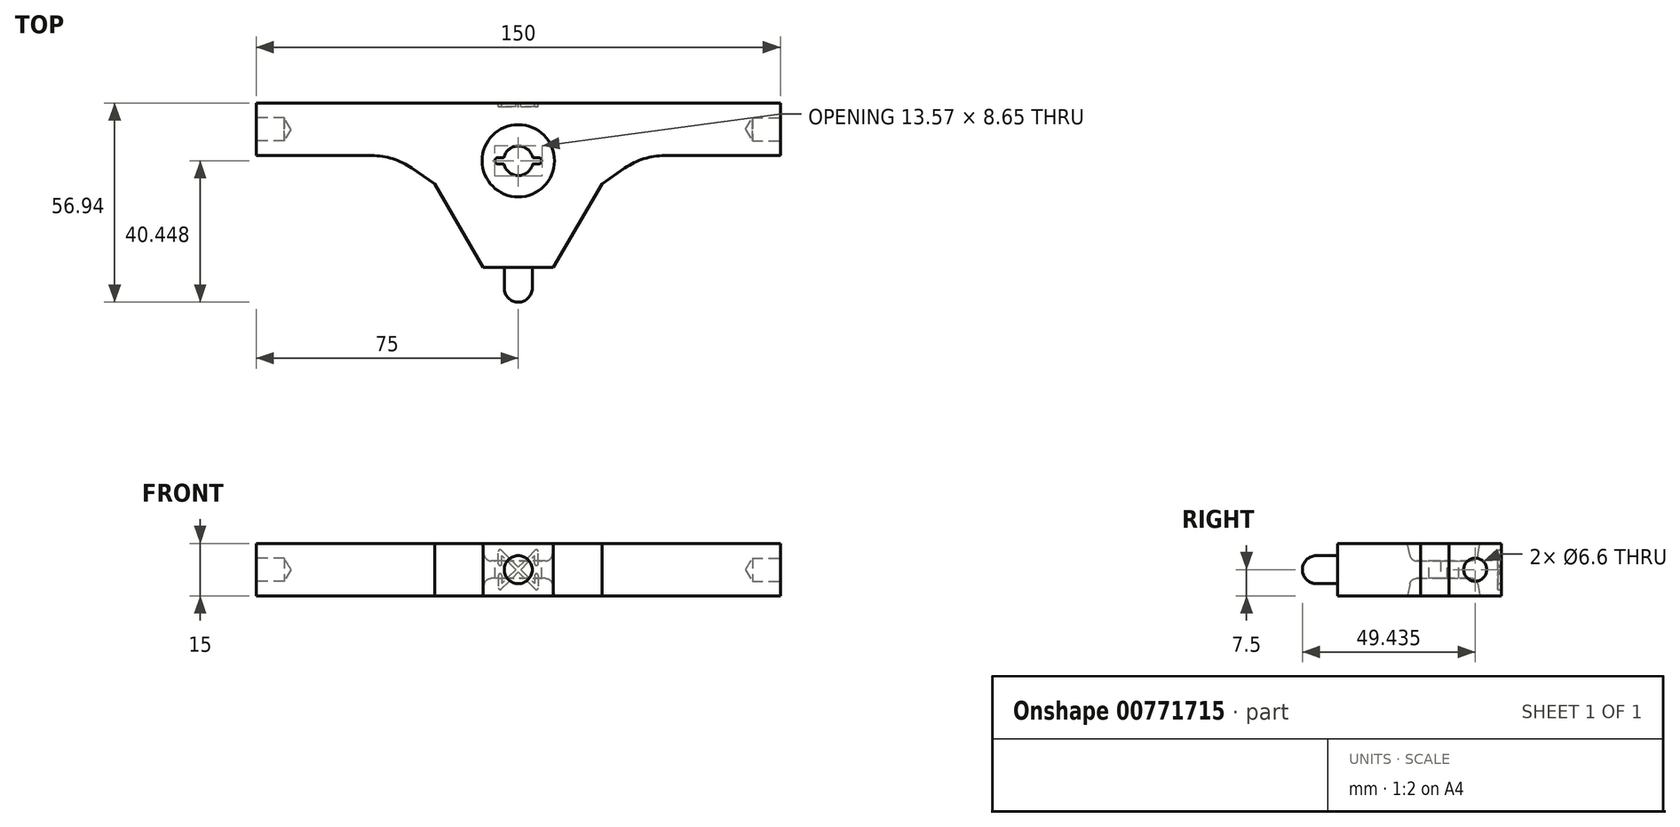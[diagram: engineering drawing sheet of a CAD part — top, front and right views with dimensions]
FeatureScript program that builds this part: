
annotation { "Feature Type Name" : "Feature", "Feature Type Description" : "" }
export const myFeature = defineFeature(function(context is Context, id is Id, definition is map)
    precondition{}
    {
        {
            var Q0;
            Q0=qCreatedBy(makeId("Top.planeOp"),FACE);
            var sketch = newSketch(context, id + "F0", { "sketchPlane" : qUnion([Q0])});
            skLineSegment(sketch, "E0", {"start": v(0, -21.97) * mm, "end": v(0, 24.97) * mm});
            skLineSegment(sketch, "E1", {"start": v(0, 24.97) * mm, "end": v(-75, 24.97) * mm});
            skLineSegment(sketch, "E2", {"start": v(-75, 24.97) * mm, "end": v(-75, 9.97) * mm});
            skLineSegment(sketch, "E3", {"start": v(-75, 9.97) * mm, "end": v(-41.9, 9.97) * mm});
            skLineSegment(sketch, "E4", {"start": v(-30.5, 6.4) * mm, "end": v(-23.93, 1.83) * mm});
            skLineSegment(sketch, "E5", {"start": v(-23.93, 1.83) * mm, "end": v(-10, -21.97) * mm});
            skLineSegment(sketch, "E6", {"start": v(-10, -21.97) * mm, "end": v(0, -21.97) * mm});
            skPoint(sketch, "E7.visualSharp", {"position": v(-35.65, 9.97) * mm});
            skArc(sketch, "E7.filletArc", {"start": v(-30.5, 6.4) * mm, "mid": v(-35.94, 9.05) * mm, "end": v(-41.9, 9.97) * mm});
            skSolve(sketch);
        }
        {
            var Q0;
            Q0=makeQuery(id+"F0.imprint","IMPRINT",FACE,{"disambiguationData":[TD([[makeQuery(id+"F0.imprint","IMPRINT",EDGE,{"derivedFrom":sQuery(id+"F0.wireOp",EDGE,"E0")}),1.0]])]});
            extrude(context, id + "F1", {"entities" : qUnion([Q0]), "depth" : 7.5 * mm, "offsetDistance" : 25 * mm});
        }
        {
            var Q0;
            {var subQ0=makeQuery(id+"F1.opExtrude","CAP_FACE",FACE,{"disambiguationData":[OSD([sQuery(id+"F0.wireOp",EDGE,"E0"),sQuery(id+"F0.wireOp",EDGE,"E1"),sQuery(id+"F0.wireOp",EDGE,"fScvAhHL-oJWp-r7Os-fa1W-G4JxEFpX7qid"),sQuery(id+"F0.wireOp",EDGE,"pbYWTiUK-muT5-LVJ1-xngA-PtOKNFyqXju7"),sQuery(id+"F0.wireOp",EDGE,"E2"),sQuery(id+"F0.wireOp",EDGE,"E3"),sQuery(id+"F0.wireOp",EDGE,"E4"),sQuery(id+"F0.wireOp",EDGE,"E5"),sQuery(id+"F0.wireOp",EDGE,"E6"),sQuery(id+"F0.wireOp",EDGE,"E7.filletArc")])],"isStart":false});Q0=makeQuery(id+"F10.boolean.opBoolean","MERGE",FACE,{"derivedFrom":[subQ0,makeQuery(id+"F10.opPattern","COPY",FACE,{"derivedFrom":subQ0,"instanceName":"1"})]});}
            var sketch = newSketch(context, id + "F2", { "sketchPlane" : qUnion([Q0])});
            skCircle(sketch, "E8", {"center": v(0, 8.48) * mm, "radius": 10.34 * mm});
            skLineSegment(sketch, "E9", {"start": v(-37.5, 24.97) * mm, "end": v(0, 8.48) * mm, "construction": true});
            skSolve(sketch);
        }
        {
            var Q0;
            Q0=makeQuery(id+"F2.imprint","IMPRINT",FACE,{"disambiguationData":[TD([[makeQuery(id+"F2.imprint","IMPRINT",EDGE,{"derivedFrom":sQuery(id+"F2.wireOp",EDGE,"E8")}),-1.0]])]});
            cPlane(context, id + "F3", {"entities" : qUnion([Q0]), "cplaneType" : CPlaneType.OFFSET, "offset" : 5 * mm, "oppositeDirection" : true, "width" : 150 * mm, "height" : 150 * mm});
        }
        {
            var Q0;
            Q0=qCreatedBy(id+"F3.planeOp",FACE);
            var sketch = newSketch(context, id + "F4", { "sketchPlane" : qUnion([Q0])});
            skCircle(sketch, "E10", {"center": v(0, 8.48) * mm, "radius": 9.45 * mm});
            skSolve(sketch);
        }
        {
            var Q1;
            Q1=makeQuery(id+"F2.imprint","IMPRINT",FACE,{"disambiguationData":[TD([[makeQuery(id+"F2.imprint","IMPRINT",EDGE,{"derivedFrom":sQuery(id+"F2.wireOp",EDGE,"E8")}),1.0]])]});
            var Q2;
            Q2 = qSketchRegion(id + "F4", true);
            loft(context, id + "F5", {"operationType" : NewBodyOperationType.REMOVE, "sheetProfilesArray" : [{ "sheetProfileEntities" : qUnion([Q1]) }, { "sheetProfileEntities" : qUnion([Q2]) }]});
        }
        {
            var Q0;
            Q0=makeQuery(id+"F5.boolean.opBoolean","COPY",EDGE,{"derivedFrom":makeQuery(id+"F5.opLoft","MID_CAP_EDGE",EDGE,{"disambiguationData":[OSD([sQuery(id+"F2.wireOp",EDGE,"E8")])],"capPos":0.0})});
            var Q1;
            Q1=makeQuery(id+"F5.boolean.opBoolean","COPY",EDGE,{"derivedFrom":makeQuery(id+"F5.opLoft","MID_CAP_EDGE",EDGE,{"disambiguationData":[OSD([sQuery(id+"F4.wireOp",EDGE,"E10")])],"capPos":1.0})});
            fillet(context, id + "F6", {"entities" : qUnion([Q0, Q1]), "radius" : 2 * mm, "tangentPropagation" : true, "allowEdgeOverflow" : false});
        }
        {
            var Q0;
            Q0=makeQuery(id+"F1.opExtrude","SWEPT_BODY",BODY,{"disambiguationData":[OSD([sQuery(id+"F0.wireOp",EDGE,"E0"),sQuery(id+"F0.wireOp",EDGE,"E1"),sQuery(id+"F0.wireOp",EDGE,"fScvAhHL-oJWp-r7Os-fa1W-G4JxEFpX7qid"),sQuery(id+"F0.wireOp",EDGE,"pbYWTiUK-muT5-LVJ1-xngA-PtOKNFyqXju7"),sQuery(id+"F0.wireOp",EDGE,"E2"),sQuery(id+"F0.wireOp",EDGE,"E3"),sQuery(id+"F0.wireOp",EDGE,"E4"),sQuery(id+"F0.wireOp",EDGE,"E5"),sQuery(id+"F0.wireOp",EDGE,"E6"),sQuery(id+"F0.wireOp",EDGE,"E7.filletArc")])]});
            var Q1;
            Q1=qCreatedBy(makeId("Top.planeOp"),FACE);
            mirror(context, id + "F7", {"operationType" : NewBodyOperationType.ADD, "entities" : qUnion([Q0]), "mirrorPlane" : qUnion([Q1])});
        }
        {
            var Q0;
            Q0=makeQuery(id+"F1.opExtrude","SWEPT_FACE",FACE,{"disambiguationData":[OSD([sQuery(id+"F0.wireOp",EDGE,"E2")])]});
            var sketch = newSketch(context, id + "F8", { "sketchPlane" : qUnion([Q0])});
            skLineSegment(sketch, "E11", {"start": v(-24.97, 0) * mm, "end": v(-17.47, 0) * mm, "construction": true});
            skPoint(sketch, "E11.endSnap0", {"position": v(-17.47, 7.5) * mm});
            skLineSegment(sketch, "E12", {"start": v(-17.47, 0) * mm, "end": v(-17.47, 7.5) * mm, "construction": true});
            skSolve(sketch);
        }
        {
            var Q0;
            Q0=sQuery(id+"F8.wireOp",VERTEX,"E11.end");
            var Q1;
            Q1=makeQuery(id+"F1.opExtrude","SWEPT_BODY",BODY,{"disambiguationData":[OSD([sQuery(id+"F0.wireOp",EDGE,"E0"),sQuery(id+"F0.wireOp",EDGE,"E1"),sQuery(id+"F0.wireOp",EDGE,"fScvAhHL-oJWp-r7Os-fa1W-G4JxEFpX7qid"),sQuery(id+"F0.wireOp",EDGE,"pbYWTiUK-muT5-LVJ1-xngA-PtOKNFyqXju7"),sQuery(id+"F0.wireOp",EDGE,"E2"),sQuery(id+"F0.wireOp",EDGE,"E3"),sQuery(id+"F0.wireOp",EDGE,"E4"),sQuery(id+"F0.wireOp",EDGE,"E5"),sQuery(id+"F0.wireOp",EDGE,"E6"),sQuery(id+"F0.wireOp",EDGE,"E7.filletArc")])]});
            hole(context, id + "F9", {"style" : HoleStyle.SIMPLE, "endStyle" : HoleEndStyle.BLIND, "standardTappedOrClearance" : lookupTablePath({ "standard" : "ISO", "fit" : "Normal", "size" : "M6", "type" : "Clearance" }), "standardBlindInLast" : lookupTablePath({ "fit" : "Standard", "standard" : "ISO", "size" : "M6", "type" : "Clearance" }), "holeDiameter" : 6.6 * mm, "majorDiameter" : 5 * mm, "holeDepth" : 8 * mm, "isTappedThrough" : true, "tappedDepth" : 12 * mm, "tapClearance" : 3, "locations" : qUnion([Q0]), "scope" : qUnion([Q1])});
        }
        {
            var Q0;
            Q0=makeQuery(id+"F1.opExtrude","SWEPT_BODY",BODY,{"disambiguationData":[OSD([sQuery(id+"F0.wireOp",EDGE,"E0"),sQuery(id+"F0.wireOp",EDGE,"E1"),sQuery(id+"F0.wireOp",EDGE,"fScvAhHL-oJWp-r7Os-fa1W-G4JxEFpX7qid"),sQuery(id+"F0.wireOp",EDGE,"pbYWTiUK-muT5-LVJ1-xngA-PtOKNFyqXju7"),sQuery(id+"F0.wireOp",EDGE,"E2"),sQuery(id+"F0.wireOp",EDGE,"E3"),sQuery(id+"F0.wireOp",EDGE,"E4"),sQuery(id+"F0.wireOp",EDGE,"E5"),sQuery(id+"F0.wireOp",EDGE,"E6"),sQuery(id+"F0.wireOp",EDGE,"E7.filletArc")])]});
            var Q1;
            Q1=qCreatedBy(makeId("Right.planeOp"),FACE);
            mirror(context, id + "F10", {"operationType" : NewBodyOperationType.ADD, "entities" : qUnion([Q0]), "mirrorPlane" : qUnion([Q1])});
        }
        {
            var Q0;
            {var subQ0=makeQuery(id+"F1.opExtrude","SWEPT_FACE",FACE,{"disambiguationData":[OSD([sQuery(id+"F0.wireOp",EDGE,"E6")])]});Q0=makeQuery(id+"F10.boolean.opBoolean","MERGE",FACE,{"derivedFrom":[subQ0,makeQuery(id+"F10.opPattern","COPY",FACE,{"derivedFrom":subQ0,"instanceName":"1"})]});}
            var sketch = newSketch(context, id + "F11", { "sketchPlane" : qUnion([Q0])});
            skLineSegment(sketch, "E13", {"start": v(-10, 0) * mm, "end": v(10, 0) * mm, "construction": true});
            skLineSegment(sketch, "E14", {"start": v(0, 7.5) * mm, "end": v(0, -7.5) * mm, "construction": true});
            skCircle(sketch, "E15", {"center": v(0, 0) * mm, "radius": 4 * mm});
            skSolve(sketch);
        }
        {
            var Q0;
            Q0=makeQuery(id+"F11.imprint","IMPRINT",FACE,{"disambiguationData":[TD([[makeQuery(id+"F11.imprint","IMPRINT",EDGE,{"derivedFrom":sQuery(id+"F11.wireOp",EDGE,"E15")}),1.0]])]});
            extrude(context, id + "F12", {"entities" : qUnion([Q0]), "operationType" : NewBodyOperationType.ADD, "depth" : 10 * mm, "offsetDistance" : 25 * mm});
        }
        {
            var Q0;
            Q0=makeQuery(id+"F12.opExtrude","CAP_FACE",FACE,{"disambiguationData":[OSD([sQuery(id+"F11.wireOp",EDGE,"E15")])],"isStart":false});
            fillet(context, id + "F13", {"entities" : qUnion([Q0]), "radius" : 4 * mm, "tangentPropagation" : true, "allowEdgeOverflow" : false});
        }
        {
            var Q0;
            {var subQ0=makeQuery(id+"F5.boolean.opBoolean","COPY",FACE,{"derivedFrom":makeQuery(id+"F5.opLoft","CAP_FACE",FACE,{"disambiguationData":[OSD([makeQuery(id+"F4.imprint","IMPRINT",FACE,{"disambiguationData":[TD([[makeQuery(id+"F4.imprint","IMPRINT",EDGE,{"derivedFrom":sQuery(id+"F4.wireOp",EDGE,"E10")}),1.0]])]})])],"isStart":true})});Q0=makeQuery(id+"F10.boolean.opBoolean","MERGE",FACE,{"derivedFrom":[subQ0,makeQuery(id+"F10.opPattern","COPY",FACE,{"derivedFrom":subQ0,"instanceName":"1"})]});}
            var sketch = newSketch(context, id + "F14", { "sketchPlane" : qUnion([Q0])});
            skArc(sketch, "E16", {"start": v(-4.12, 7.54) * mm, "mid": v(0, 4.25) * mm, "end": v(4.12, 7.54) * mm});
            skLineSegment(sketch, "E17.bottom", {"start": v(5.74, 9.42) * mm, "end": v(4.12, 9.42) * mm});
            skLineSegment(sketch, "E17.top", {"start": v(5.74, 7.54) * mm, "end": v(4.12, 7.54) * mm});
            skArc(sketch, "E18", {"start": v(-5.74, 9.42) * mm, "mid": v(-6.68, 8.48) * mm, "end": v(-5.74, 7.54) * mm});
            skArc(sketch, "E19", {"start": v(5.74, 7.54) * mm, "mid": v(6.68, 8.48) * mm, "end": v(5.74, 9.42) * mm});
            skLineSegment(sketch, "E20.trimOffspring", {"start": v(-4.12, 9.42) * mm, "end": v(-5.74, 9.42) * mm});
            skLineSegment(sketch, "E21.trimOffspring", {"start": v(-4.12, 7.54) * mm, "end": v(-5.74, 7.54) * mm});
            skArc(sketch, "E22.trimOffspring", {"start": v(4.12, 9.42) * mm, "mid": v(0, 12.7) * mm, "end": v(-4.12, 9.42) * mm});
            skSolve(sketch);
        }
        {
            var Q0;
            Q0 = qSketchRegion(id + "F14", true);
            extrude(context, id + "F15", {"entities" : qUnion([Q0]), "operationType" : NewBodyOperationType.REMOVE, "endBound" : BoundingType.THROUGH_ALL, "oppositeDirection" : true, "depth" : 25 * mm, "offsetDistance" : 25 * mm});
        }
        {
            var Q0;
            Q0=makeQuery(id+"F15.boolean.opBoolean","COPY",FACE,{"derivedFrom":makeQuery(id+"F15.opExtrude","SWEPT_FACE",FACE,{"disambiguationData":[OSD([sQuery(id+"F14.wireOp",EDGE,"E22.trimOffspring")])]})});
            var Q1;
            Q1=makeQuery(id+"F15.boolean.opBoolean","COPY",FACE,{"derivedFrom":makeQuery(id+"F15.opExtrude","SWEPT_FACE",FACE,{"disambiguationData":[OSD([sQuery(id+"F14.wireOp",EDGE,"E20.trimOffspring")])]})});
            var Q2;
            Q2=makeQuery(id+"F15.boolean.opBoolean","COPY",FACE,{"derivedFrom":makeQuery(id+"F15.opExtrude","SWEPT_FACE",FACE,{"disambiguationData":[OSD([sQuery(id+"F14.wireOp",EDGE,"E16")])]})});
            var Q3;
            Q3=makeQuery(id+"F15.boolean.opBoolean","COPY",FACE,{"derivedFrom":makeQuery(id+"F15.opExtrude","SWEPT_FACE",FACE,{"disambiguationData":[OSD([sQuery(id+"F14.wireOp",EDGE,"E19")])]})});
            fillet(context, id + "F16", {"entities" : qUnion([Q0, Q1, Q2, Q3]), "radius" : 0.1 * mm, "tangentPropagation" : true, "allowEdgeOverflow" : false});
        }
        {
            var Q0;
            {var subQ0=makeQuery(id+"F1.opExtrude","SWEPT_FACE",FACE,{"disambiguationData":[OSD([sQuery(id+"F0.wireOp",EDGE,"E1")])]});var subQ1=makeQuery(id+"F7.boolean.opBoolean","MERGE",FACE,{"derivedFrom":[subQ0,makeQuery(id+"F7.opPattern","COPY",FACE,{"derivedFrom":subQ0,"instanceName":"1"})]});Q0=makeQuery(id+"F10.boolean.opBoolean","MERGE",FACE,{"derivedFrom":[subQ1,makeQuery(id+"F10.opPattern","COPY",FACE,{"derivedFrom":subQ1,"instanceName":"1"})]});}
            var sketch = newSketch(context, id + "F17", { "sketchPlane" : qUnion([Q0])});
            skLineSegment(sketch, "E23", {"start": v(-5.7, 1.7) * mm, "end": v(-5.7, 5.2) * mm});
            skLineSegment(sketch, "E24", {"start": v(-4.7, 1.7) * mm, "end": v(-4.7, 3.99) * mm});
            skArc(sketch, "E25", {"start": v(-5.7, 1.7) * mm, "mid": v(-5.2, 1.2) * mm, "end": v(-4.7, 1.7) * mm});
            skArc(sketch, "E26", {"start": v(-4.84, 5.55) * mm, "mid": v(-5.39, 5.66) * mm, "end": v(-5.7, 5.2) * mm});
            skLineSegment(sketch, "E27", {"start": v(-4.84, 5.55) * mm, "end": v(0, 0.7) * mm});
            skLineSegment(sketch, "E28", {"start": v(-0.7, 0) * mm, "end": v(-4.7, 3.99) * mm});
            skArc(sketch, "E29.MirrorCS", {"start": v(4.84, 5.55) * mm, "mid": v(5.39, 5.66) * mm, "end": v(5.7, 5.2) * mm});
            skLineSegment(sketch, "E30.MirrorCS", {"start": v(4.7, 1.7) * mm, "end": v(4.7, 3.99) * mm});
            skArc(sketch, "E31.MirrorCS", {"start": v(5.7, 1.7) * mm, "mid": v(5.2, 1.2) * mm, "end": v(4.7, 1.7) * mm});
            skLineSegment(sketch, "E32.MirrorCS", {"start": v(0.7, 0) * mm, "end": v(4.7, 3.99) * mm});
            skLineSegment(sketch, "E33.MirrorCS", {"start": v(5.7, 1.7) * mm, "end": v(5.7, 5.2) * mm});
            skLineSegment(sketch, "E34.MirrorCS", {"start": v(4.84, 5.55) * mm, "end": v(0, 0.7) * mm});
            skLineSegment(sketch, "E35.MirrorCS", {"start": v(-0.7, 0) * mm, "end": v(-4.7, -3.99) * mm});
            skLineSegment(sketch, "E36.MirrorCS", {"start": v(4.84, -5.55) * mm, "end": v(0, -0.7) * mm});
            skLineSegment(sketch, "E37.MirrorCS", {"start": v(-4.84, -5.55) * mm, "end": v(0, -0.7) * mm});
            skLineSegment(sketch, "E38.MirrorCS", {"start": v(0.7, 0) * mm, "end": v(4.7, -3.99) * mm});
            skArc(sketch, "E39.MirrorCS", {"start": v(-5.7, -1.7) * mm, "mid": v(-5.2, -1.2) * mm, "end": v(-4.7, -1.7) * mm});
            skArc(sketch, "E40.MirrorCS", {"start": v(4.84, -5.55) * mm, "mid": v(5.39, -5.66) * mm, "end": v(5.7, -5.2) * mm});
            skArc(sketch, "E41.MirrorCS", {"start": v(-4.84, -5.55) * mm, "mid": v(-5.39, -5.66) * mm, "end": v(-5.7, -5.2) * mm});
            skLineSegment(sketch, "E42.MirrorCS", {"start": v(4.7, -1.7) * mm, "end": v(4.7, -3.99) * mm});
            skArc(sketch, "E43.MirrorCS", {"start": v(5.7, -1.7) * mm, "mid": v(5.2, -1.2) * mm, "end": v(4.7, -1.7) * mm});
            skLineSegment(sketch, "E44.MirrorCS", {"start": v(-5.7, -1.7) * mm, "end": v(-5.7, -5.2) * mm});
            skLineSegment(sketch, "E45.MirrorCS", {"start": v(5.7, -1.7) * mm, "end": v(5.7, -5.2) * mm});
            skLineSegment(sketch, "E46.MirrorCS", {"start": v(-4.7, -1.7) * mm, "end": v(-4.7, -3.99) * mm});
            skPoint(sketch, "E47.orphan", {"position": v(0, 0.7) * mm});
            skPoint(sketch, "E48.orphan", {"position": v(0, -0.7) * mm});
            skSolve(sketch);
        }
        {
            var Q0;
            Q0=makeQuery(id+"F17.imprint","IMPRINT",FACE,{"disambiguationData":[TD([[makeQuery(id+"F17.imprint","IMPRINT",EDGE,{"derivedFrom":sQuery(id+"F17.wireOp",EDGE,"E23")}),-1.0]])]});
            extrude(context, id + "F18", {"entities" : qUnion([Q0]), "operationType" : NewBodyOperationType.REMOVE, "oppositeDirection" : true, "depth" : 1 * mm, "offsetDistance" : 25 * mm});
        }
    });
